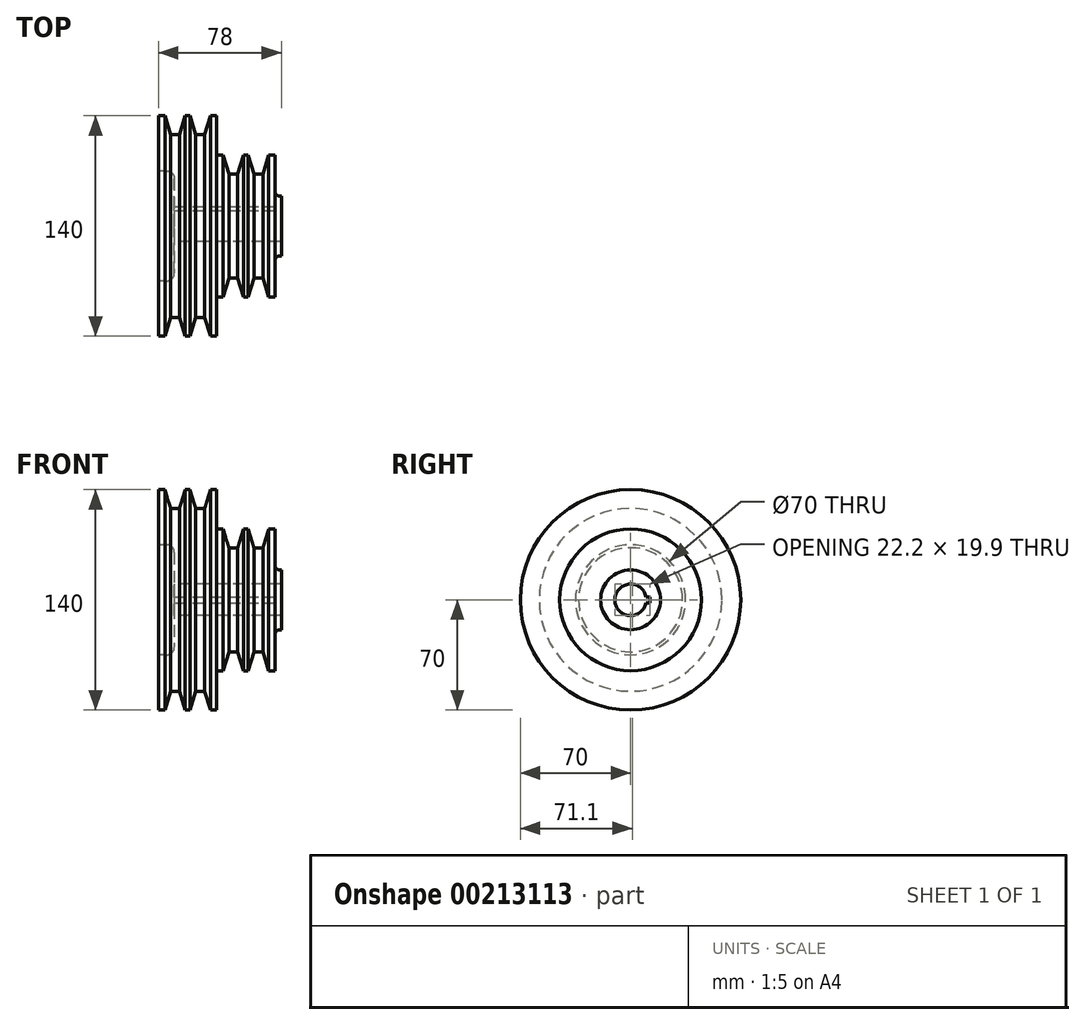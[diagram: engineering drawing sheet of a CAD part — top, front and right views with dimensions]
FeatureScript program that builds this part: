
annotation { "Feature Type Name" : "Feature", "Feature Type Description" : "" }
export const myFeature = defineFeature(function(context is Context, id is Id, definition is map)
    precondition{}
    {
        {
            var Q0;
            Q0=qCreatedBy(makeId("Front.planeOp"),FACE);
            var sketch = newSketch(context, id + "F0", { "sketchPlane" : qUnion([Q0])});
            skLineSegment(sketch, "E0", {"start": v(-57.85, 0) * mm, "end": v(61.1, 0) * mm, "construction": true});
            skLineSegment(sketch, "E1", {"start": v(41, 10) * mm, "end": v(41, 19) * mm});
            skLineSegment(sketch, "E2", {"start": v(41, 19) * mm, "end": v(40, 19) * mm});
            skLineSegment(sketch, "E3", {"start": v(37, 22) * mm, "end": v(37, 45) * mm});
            skLineSegment(sketch, "E4", {"start": v(37, 45) * mm, "end": v(33, 45) * mm});
            skLineSegment(sketch, "E5", {"start": v(33, 45) * mm, "end": v(29.35, 33.05) * mm});
            skLineSegment(sketch, "E6", {"start": v(29.35, 33.05) * mm, "end": v(23.65, 33.05) * mm});
            skLineSegment(sketch, "E7", {"start": v(23.65, 33.05) * mm, "end": v(20, 45) * mm});
            skLineSegment(sketch, "E8", {"start": v(20, 45) * mm, "end": v(17, 45) * mm});
            skLineSegment(sketch, "E9", {"start": v(17, 45) * mm, "end": v(13.35, 33.05) * mm});
            skLineSegment(sketch, "E10", {"start": v(13.35, 33.05) * mm, "end": v(7.65, 33.05) * mm});
            skLineSegment(sketch, "E11", {"start": v(7.65, 33.05) * mm, "end": v(4, 45) * mm});
            skLineSegment(sketch, "E12", {"start": v(4, 45) * mm, "end": v(0, 45) * mm});
            skLineSegment(sketch, "E13", {"start": v(0, 45) * mm, "end": v(0, 70) * mm});
            skLineSegment(sketch, "E14", {"start": v(0, 70) * mm, "end": v(-4, 70) * mm});
            skLineSegment(sketch, "E15", {"start": v(-4, 70) * mm, "end": v(-7.65, 58.05) * mm});
            skLineSegment(sketch, "E16", {"start": v(-7.65, 58.05) * mm, "end": v(-13.35, 58.05) * mm});
            skLineSegment(sketch, "E17", {"start": v(-13.35, 58.05) * mm, "end": v(-17, 70) * mm});
            skLineSegment(sketch, "E18", {"start": v(-17, 70) * mm, "end": v(-20, 70) * mm});
            skLineSegment(sketch, "E19", {"start": v(-23.65, 58.05) * mm, "end": v(-20, 70) * mm});
            skLineSegment(sketch, "E20", {"start": v(-23.65, 58.05) * mm, "end": v(-29.35, 58.05) * mm});
            skLineSegment(sketch, "E21", {"start": v(-33, 70) * mm, "end": v(-29.35, 58.05) * mm});
            skLineSegment(sketch, "E22", {"start": v(-33, 70) * mm, "end": v(-37, 70) * mm});
            skLineSegment(sketch, "E23", {"start": v(-37, 70) * mm, "end": v(-37, 35) * mm});
            skLineSegment(sketch, "E24", {"start": v(-27, 10) * mm, "end": v(41, 10) * mm});
            skLineSegment(sketch, "E25", {"start": v(-37, 35) * mm, "end": v(-32, 35) * mm});
            skLineSegment(sketch, "E26", {"start": v(-27, 30) * mm, "end": v(-27, 10) * mm});
            skPoint(sketch, "E27.orphan", {"position": v(-37, 10) * mm});
            skPoint(sketch, "E28.visualSharp", {"position": v(-27, 35) * mm});
            skArc(sketch, "E28.filletArc", {"start": v(-27, 30) * mm, "mid": v(-28.46, 33.54) * mm, "end": v(-32, 35) * mm});
            skPoint(sketch, "E29.visualSharp", {"position": v(37, 19) * mm});
            skArc(sketch, "E29.filletArc", {"start": v(37, 22) * mm, "mid": v(37.88, 19.88) * mm, "end": v(40, 19) * mm});
            skSolve(sketch);
        }
        {
            var Q0;
            Q0=makeQuery(id+"F0.imprint","IMPRINT",FACE,{"disambiguationData":[TD([[makeQuery(id+"F0.imprint","IMPRINT",EDGE,{"derivedFrom":sQuery(id+"F0.wireOp",EDGE,"E1")}),1.0]])]});
            var Q1;
            Q1=sQuery(id+"F0.wireOp",EDGE,"E0");
            revolve(context, id + "F1", {"entities" : qUnion([Q0]), "axis" : qUnion([Q1]), "revolveType" : RevolveType.FULL});
        }
        {
            var Q0;
            Q0=makeQuery(id+"F1.opRevolve","SWEPT_FACE",FACE,{"disambiguationData":[OSD([sQuery(id+"F0.wireOp",EDGE,"E1")])]});
            var sketch = newSketch(context, id + "F2", { "sketchPlane" : qUnion([Q0])});
            skArc(sketch, "E30.0", {"start": v(9.8, -2) * mm, "mid": v(10, 0) * mm, "end": v(9.8, 2) * mm});
            skLineSegment(sketch, "E31", {"start": v(9.8, 2) * mm, "end": v(12.2, 2) * mm});
            skLineSegment(sketch, "E32", {"start": v(12.2, 2) * mm, "end": v(12.2, -2) * mm});
            skLineSegment(sketch, "E33", {"start": v(12.2, -2) * mm, "end": v(9.8, -2) * mm});
            skSolve(sketch);
        }
        {
            var Q0;
            Q0=makeQuery(id+"F2.imprint","IMPRINT",FACE,{"disambiguationData":[TD([[makeQuery(id+"F2.imprint","IMPRINT",EDGE,{"derivedFrom":sQuery(id+"F2.wireOp",EDGE,"E30.0")}),1.0]])]});
            extrude(context, id + "F3", {"entities" : qUnion([Q0]), "operationType" : NewBodyOperationType.REMOVE, "endBound" : BoundingType.THROUGH_ALL, "oppositeDirection" : true, "depth" : 25 * mm});
        }
    });
